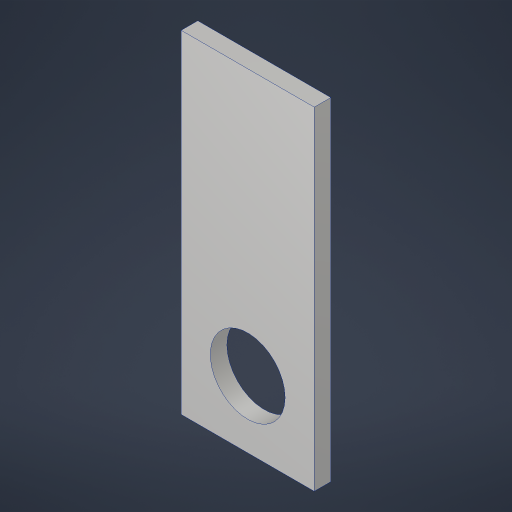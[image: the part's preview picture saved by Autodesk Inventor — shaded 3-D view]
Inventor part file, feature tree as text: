
AUTODESK INVENTOR PART (.ipt)
format: ipt  version: 2023.4 (Build 274418000, 418)  size: 179,200 bytes
history: native  units: in
note: dims shown in document units (in); Inventor stores cm internally (conversion verified against a paired STEP export)
features: extrude x1, hole x1, sketch x1, projected_geometry x1
ambient origin geometry x8: Origin, YZ Plane, XZ Plane, XY Plane, X Axis, Y Axis, Z Axis, Center Point
bodies: Solid1 (feature_tree)
feature tree (4):
  extrude  "Extrusion1"  Depth=0.25in
  hole  "Hole1"  [1 undecoded]
  sketch  "Sketch2"  dims[d3=0.0in d4=1.0in d5=1.125in d6=0.75in d7=0.385in d8=0.25in d9=0.5635in d10=1.0in d11=0.8108in]
  projected_geometry  "Project Cut Edges1"
note: 1 required parameter value undecoded (feature->parameter linkage not recoverable at this tier; creation-order binding heuristic only, values carry confidence <= 0.55)
